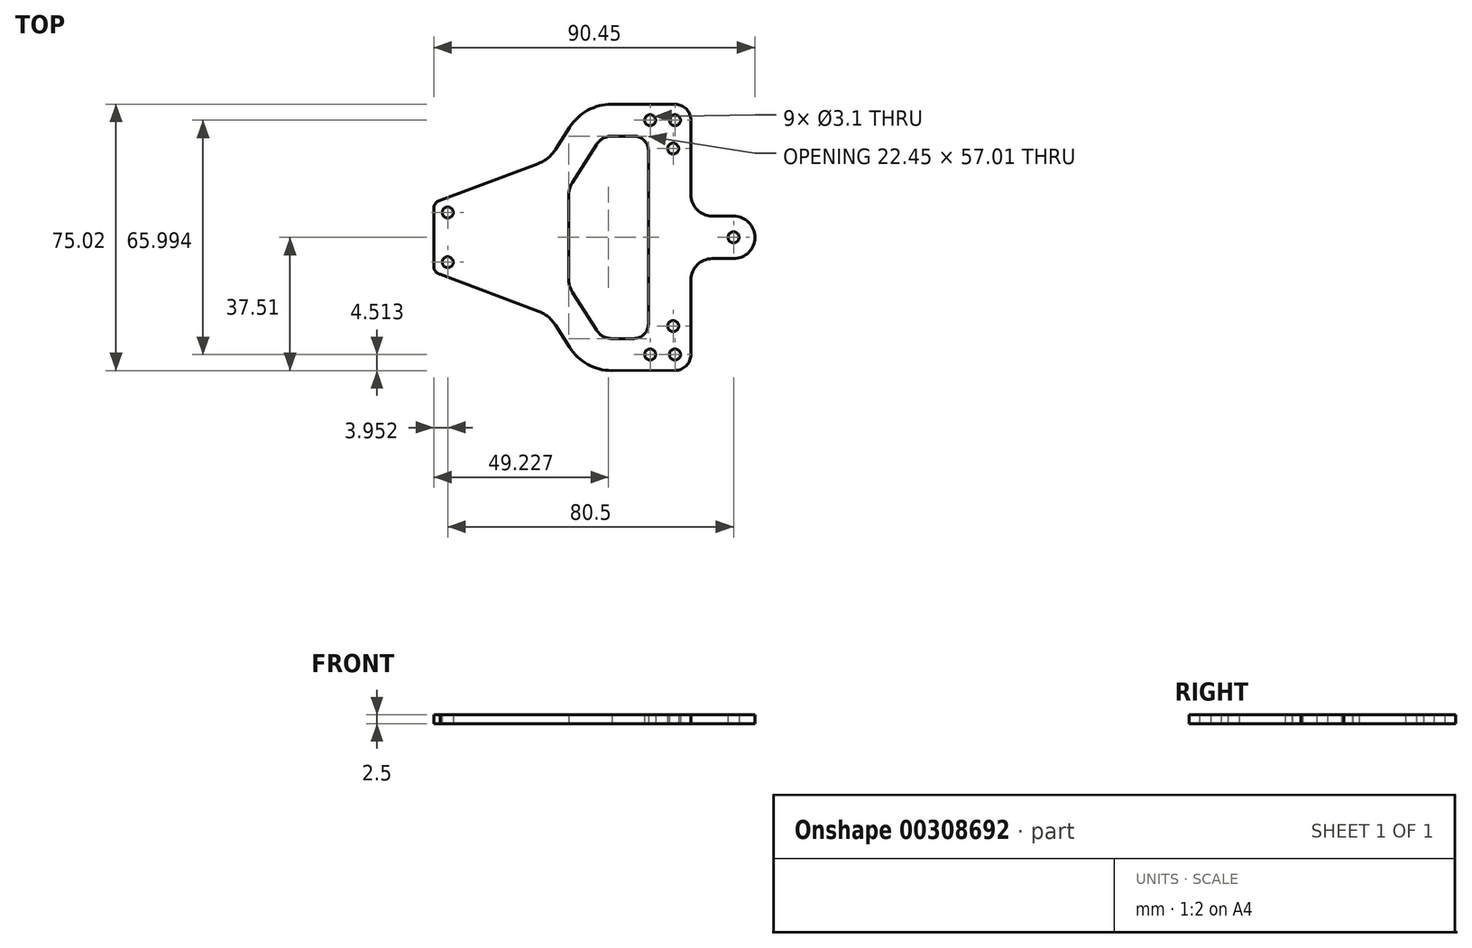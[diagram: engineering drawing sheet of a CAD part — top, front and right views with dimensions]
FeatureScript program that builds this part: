
annotation { "Feature Type Name" : "Feature", "Feature Type Description" : "" }
export const myFeature = defineFeature(function(context is Context, id is Id, definition is map)
    precondition{}
    {
        {
            var Q0;
            Q0=qCreatedBy(makeId("Top.planeOp"),FACE);
            var sketch = newSketch(context, id + "F0", { "sketchPlane" : qUnion([Q0])});
            skLineSegment(sketch, "E0.bottom", {"start": v(0, 0) * mm, "end": v(0, 0) * mm});
            skLineSegment(sketch, "E0.top", {"start": v(0, 0) * mm, "end": v(0, 0) * mm});
            skLineSegment(sketch, "E0.left", {"start": v(0, 0) * mm, "end": v(0, 0) * mm});
            skLineSegment(sketch, "E0.right", {"start": v(0, 0) * mm, "end": v(0, 0) * mm});
            skPoint(sketch, "E1.middle", {"position": v(0, 0) * mm});
            skArc(sketch, "E2.filletArc", {"start": v(24.13, 33) * mm, "mid": v(22.8, 36.18) * mm, "end": v(19.64, 37.5) * mm});
            skCircle(sketch, "E3", {"center": v(19.63, 33) * mm, "radius": 1.55 * mm});
            skCircle(sketch, "E4", {"center": v(12.63, 33) * mm, "radius": 1.55 * mm});
            skCircle(sketch, "E5", {"center": v(-44.37, 7) * mm, "radius": 1.55 * mm});
            skArc(sketch, "E6.filletArc", {"start": v(-46.53, 10.41) * mm, "mid": v(-47.7, 9.7) * mm, "end": v(-48.32, 8.48) * mm});
            skLineSegment(sketch, "E7", {"start": v(-48.32, 8.48) * mm, "end": v(-48.32, -8.48) * mm});
            skLineSegment(sketch, "E8", {"start": v(-2.43, 26.18) * mm, "end": v(-9.23, 15.43) * mm});
            skArc(sketch, "E9.filletArc", {"start": v(1.86, 28.5) * mm, "mid": v(-0.59, 27.9) * mm, "end": v(-2.43, 26.18) * mm});
            skLineSegment(sketch, "E10", {"start": v(-10.32, 11.69) * mm, "end": v(-10.32, -11.77) * mm});
            skArc(sketch, "E11.filletArc", {"start": v(-9.23, 15.43) * mm, "mid": v(-10.04, 13.64) * mm, "end": v(-10.32, 11.69) * mm});
            skLineSegment(sketch, "E12", {"start": v(24.13, 33) * mm, "end": v(24.13, 12) * mm});
            skPoint(sketch, "E13.visualSharp", {"position": v(-11, 37.5) * mm});
            skArc(sketch, "E14.filletArc", {"start": v(1.84, 37.5) * mm, "mid": v(-4.95, 35.77) * mm, "end": v(-10.05, 30.97) * mm});
            skLineSegment(sketch, "E15", {"start": v(1.84, 37.5) * mm, "end": v(19.64, 37.5) * mm});
            skLineSegment(sketch, "E16.MirrorCS", {"start": v(1.84, -37.5) * mm, "end": v(19.64, -37.5) * mm});
            skCircle(sketch, "E17.MirrorC", {"center": v(19.63, -33) * mm, "radius": 1.55 * mm});
            skLineSegment(sketch, "E18.MirrorCS", {"start": v(24.13, -33) * mm, "end": v(24.13, -12) * mm});
            skArc(sketch, "E19.MirrorCS", {"start": v(-46.53, -10.41) * mm, "mid": v(-47.7, -9.7) * mm, "end": v(-48.32, -8.48) * mm});
            skArc(sketch, "E20.MirrorCS", {"start": v(-9.23, -15.43) * mm, "mid": v(-10.04, -13.64) * mm, "end": v(-10.32, -11.69) * mm});
            skLineSegment(sketch, "E21.MirrorCS", {"start": v(-2.43, -26.18) * mm, "end": v(-9.23, -15.43) * mm});
            skArc(sketch, "E22.MirrorCS", {"start": v(1.86, -28.5) * mm, "mid": v(-0.59, -27.9) * mm, "end": v(-2.43, -26.18) * mm});
            skCircle(sketch, "E23.MirrorC", {"center": v(12.63, -33) * mm, "radius": 1.55 * mm});
            skCircle(sketch, "E24.MirrorC", {"center": v(-44.37, -7) * mm, "radius": 1.55 * mm});
            skCircle(sketch, "E25", {"center": v(19.13, -25) * mm, "radius": 1.55 * mm});
            skCircle(sketch, "E26.MirrorC", {"center": v(19.13, 25) * mm, "radius": 1.55 * mm});
            skCircle(sketch, "E27", {"center": v(36.13, 0) * mm, "radius": 1.55 * mm});
            skLineSegment(sketch, "E28", {"start": v(42.13, 0) * mm, "end": v(42.13, 0) * mm});
            skLineSegment(sketch, "E29", {"start": v(1.86, 28.5) * mm, "end": v(8.14, 28.5) * mm});
            skPoint(sketch, "E30.visualSharp", {"position": v(18.13, 28.5) * mm});
            skArc(sketch, "E30.filletArc", {"start": v(12.13, 24.5) * mm, "mid": v(10.96, 27.33) * mm, "end": v(8.14, 28.5) * mm});
            skLineSegment(sketch, "E31", {"start": v(1.86, -28.5) * mm, "end": v(8.13, -28.5) * mm});
            skLineSegment(sketch, "E32", {"start": v(12.13, 24.5) * mm, "end": v(12.13, -24.5) * mm});
            skPoint(sketch, "E33.visualSharp", {"position": v(12.13, -28.5) * mm});
            skArc(sketch, "E33.filletArc", {"start": v(8.13, -28.5) * mm, "mid": v(10.96, -27.33) * mm, "end": v(12.13, -24.5) * mm});
            skLineSegment(sketch, "E34", {"start": v(24.13, -12) * mm, "end": v(24.13, -12) * mm});
            skLineSegment(sketch, "E35", {"start": v(30.13, -6) * mm, "end": v(36.13, -6) * mm});
            skLineSegment(sketch, "E36", {"start": v(24.13, 12) * mm, "end": v(24.13, 12) * mm});
            skLineSegment(sketch, "E37", {"start": v(30.13, 6) * mm, "end": v(36.13, 6) * mm});
            skPoint(sketch, "E38.visualSharp", {"position": v(42.13, -6) * mm});
            skArc(sketch, "E38.filletArc", {"start": v(36.13, -6) * mm, "mid": v(40.37, -4.24) * mm, "end": v(42.13, 0) * mm});
            skPoint(sketch, "E39.visualSharp", {"position": v(42.13, 6) * mm});
            skArc(sketch, "E39.filletArc", {"start": v(42.13, 0) * mm, "mid": v(40.37, 4.24) * mm, "end": v(36.13, 6) * mm});
            skPoint(sketch, "E40.visualSharp", {"position": v(24.13, -6) * mm});
            skArc(sketch, "E40.filletArc", {"start": v(30.13, -6) * mm, "mid": v(25.89, -7.76) * mm, "end": v(24.13, -12) * mm});
            skPoint(sketch, "E41.visualSharp", {"position": v(24.13, 6) * mm});
            skArc(sketch, "E41.filletArc", {"start": v(24.13, 12) * mm, "mid": v(25.89, 7.76) * mm, "end": v(30.13, 6) * mm});
            skArc(sketch, "E42.filletArc", {"start": v(19.64, -37.5) * mm, "mid": v(22.82, -36.17) * mm, "end": v(24.13, -33) * mm});
            skLineSegment(sketch, "E43", {"start": v(-46.53, 10.41) * mm, "end": v(-18.9, 20.78) * mm});
            skLineSegment(sketch, "E44", {"start": v(-10.05, 30.97) * mm, "end": v(-13.96, 24.8) * mm});
            skArc(sketch, "E45.filletArc", {"start": v(-18.9, 20.78) * mm, "mid": v(-16.1, 22.38) * mm, "end": v(-13.96, 24.8) * mm});
            skLineSegment(sketch, "E46.MirrorCS", {"start": v(-46.53, -10.41) * mm, "end": v(-18.9, -20.78) * mm});
            skArc(sketch, "E47.MirrorCS", {"start": v(-18.9, -20.78) * mm, "mid": v(-16.1, -22.38) * mm, "end": v(-13.96, -24.8) * mm});
            skLineSegment(sketch, "E48.MirrorCS", {"start": v(-10.05, -30.97) * mm, "end": v(-13.96, -24.8) * mm});
            skArc(sketch, "E49.MirrorCS", {"start": v(1.84, -37.5) * mm, "mid": v(-4.95, -35.77) * mm, "end": v(-10.05, -30.97) * mm});
            skSolve(sketch);
        }
        {
            var Q0;
            Q0=qSketchRegion(id+"F0",true);
            extrude(context, id + "F1", {"entities" : qUnion([Q0]), "depth" : 2.5 * mm});
        }
    });
